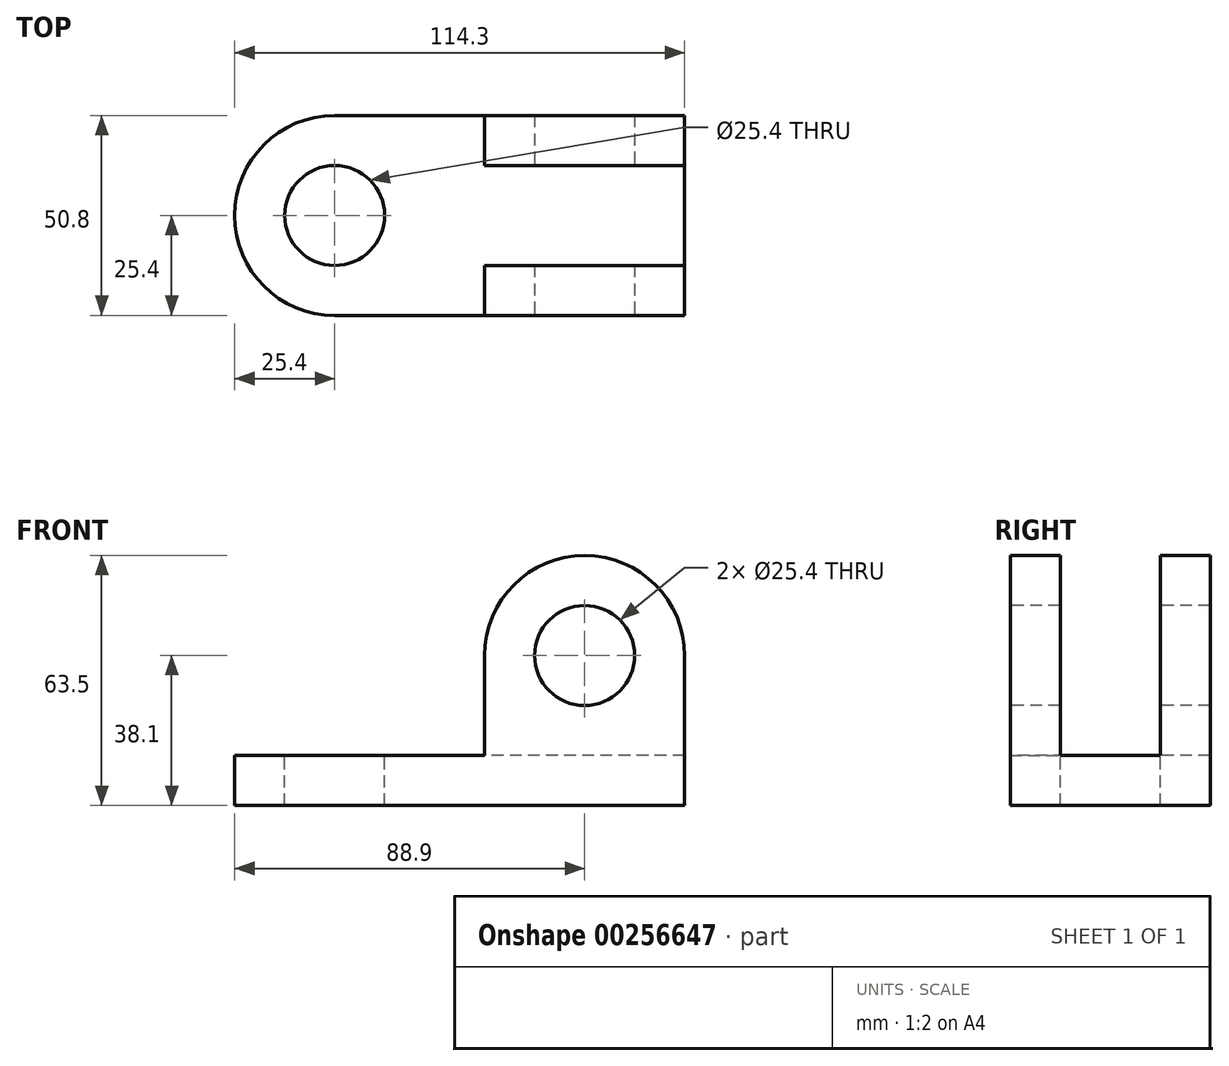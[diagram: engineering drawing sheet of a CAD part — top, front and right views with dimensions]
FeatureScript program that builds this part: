
annotation { "Feature Type Name" : "Feature", "Feature Type Description" : "" }
export const myFeature = defineFeature(function(context is Context, id is Id, definition is map)
    precondition{}
    {
        {
            var Q0;
            Q0=qCreatedBy(makeId("Top.planeOp"),FACE);
            var sketch = newSketch(context, id + "F0", { "sketchPlane" : qUnion([Q0])});
            skLineSegment(sketch, "E0.bottom", {"start": v(25.4, 0) * mm, "end": v(114.3, 0) * mm});
            skLineSegment(sketch, "E0.top", {"start": v(25.4, 50.8) * mm, "end": v(114.3, 50.8) * mm});
            skLineSegment(sketch, "E0.left", {"start": v(0, 25.4) * mm, "end": v(0, 25.4) * mm});
            skLineSegment(sketch, "E0.right", {"start": v(114.3, 0) * mm, "end": v(114.3, 50.8) * mm});
            skPoint(sketch, "E1.visualSharp", {"position": v(0, 50.8) * mm});
            skArc(sketch, "E1.filletArc", {"start": v(25.4, 50.8) * mm, "mid": v(7.44, 43.36) * mm, "end": v(0, 25.4) * mm});
            skPoint(sketch, "E2.visualSharp", {"position": v(0, 0) * mm});
            skArc(sketch, "E2.filletArc", {"start": v(0, 25.4) * mm, "mid": v(7.44, 7.44) * mm, "end": v(25.4, 0) * mm});
            skSolve(sketch);
        }
        {
            var Q0;
            Q0=makeQuery(id+"F0.imprint","IMPRINT",FACE,{"disambiguationData":[TD([[makeQuery(id+"F0.imprint","IMPRINT",EDGE,{"derivedFrom":sQuery(id+"F0.wireOp",EDGE,"E0.bottom")}),1.0]])]});
            extrude(context, id + "F1", {"entities" : qUnion([Q0]), "depth" : 12.7 * mm});
        }
        {
            var Q0;
            Q0=makeQuery(id+"F1.opExtrude","CAP_FACE",FACE,{"disambiguationData":[OSD([sQuery(id+"F0.wireOp",EDGE,"E0.bottom"),sQuery(id+"F0.wireOp",EDGE,"E0.top"),sQuery(id+"F0.wireOp",EDGE,"E0.left"),sQuery(id+"F0.wireOp",EDGE,"E0.right")])],"isStart":false});
            var sketch = newSketch(context, id + "F2", { "sketchPlane" : qUnion([Q0])});
            skLineSegment(sketch, "E3", {"start": v(0, 25.4) * mm, "end": v(114.3, 25.4) * mm, "construction": true});
            skLineSegment(sketch, "E4.bottom", {"start": v(114.3, 0) * mm, "end": v(63.5, 0) * mm});
            skLineSegment(sketch, "E4.top", {"start": v(114.3, 12.7) * mm, "end": v(63.5, 12.7) * mm});
            skLineSegment(sketch, "E4.left", {"start": v(114.3, 0) * mm, "end": v(114.3, 12.7) * mm});
            skLineSegment(sketch, "E4.right", {"start": v(63.5, 0) * mm, "end": v(63.5, 12.7) * mm});
            skLineSegment(sketch, "E5.MirrorCS", {"start": v(63.5, 50.8) * mm, "end": v(63.5, 38.1) * mm});
            skLineSegment(sketch, "E6.MirrorCS", {"start": v(114.3, 50.8) * mm, "end": v(114.3, 38.1) * mm});
            skLineSegment(sketch, "E7.MirrorCS", {"start": v(114.3, 38.1) * mm, "end": v(63.5, 38.1) * mm});
            skLineSegment(sketch, "E8.MirrorCS", {"start": v(114.3, 50.8) * mm, "end": v(63.5, 50.8) * mm});
            skPoint(sketch, "E9", {"position": v(25.4, 25.4) * mm});
            skSolve(sketch);
        }
        {
            var Q0;
            Q0=makeQuery(id+"F2.imprint","IMPRINT",FACE,{"disambiguationData":[TD([[makeQuery(id+"F2.imprint","IMPRINT",EDGE,{"derivedFrom":sQuery(id+"F2.wireOp",EDGE,"E4.bottom")}),1.0]])]});
            var Q1;
            Q1=makeQuery(id+"F2.imprint","IMPRINT",FACE,{"disambiguationData":[TD([[makeQuery(id+"F2.imprint","IMPRINT",EDGE,{"derivedFrom":sQuery(id+"F2.wireOp",EDGE,"E5.MirrorCS")}),1.0]])]});
            extrude(context, id + "F3", {"entities" : qUnion([Q0, Q1]), "operationType" : NewBodyOperationType.ADD, "depth" : 50.8 * mm});
        }
        {
            var Q0;
            Q0=sQuery(id+"F2.wireOp",VERTEX,"E9");
            var Q1;
            Q1=makeQuery(id+"F1.opExtrude","SWEPT_BODY",BODY,{"disambiguationData":[OSD([sQuery(id+"F0.wireOp",EDGE,"E0.bottom"),sQuery(id+"F0.wireOp",EDGE,"E0.top"),sQuery(id+"F0.wireOp",EDGE,"E0.right"),sQuery(id+"F0.wireOp",EDGE,"E1.filletArc"),sQuery(id+"F0.wireOp",EDGE,"E2.filletArc")])]});
            hole(context, id + "F4", {"style" : HoleStyle.SIMPLE, "endStyle" : HoleEndStyle.THROUGH, "holeDiameter" : 25.4 * mm, "tappedDepth" : 12.7 * mm, "tapClearance" : 3, "locations" : qUnion([Q0]), "scope" : qUnion([Q1])});
        }
        {
            var Q0;
            Q0=makeQuery(id+"F3.opExtrude","CAP_EDGE",EDGE,{"disambiguationData":[OSD([sQuery(id+"F2.wireOp",EDGE,"E4.right")])],"isStart":false});
            fillet(context, id + "F5", {"entities" : qUnion([Q0]), "radius" : 25.4 * mm, "tangentPropagation" : true, "allowEdgeOverflow" : false});
        }
        {
            var Q0;
            Q0=makeQuery(id+"F3.opExtrude","CAP_EDGE",EDGE,{"disambiguationData":[OSD([sQuery(id+"F2.wireOp",EDGE,"E4.left")])],"isStart":false});
            fillet(context, id + "F6", {"entities" : qUnion([Q0]), "radius" : 25.4 * mm, "tangentPropagation" : true, "allowEdgeOverflow" : false});
        }
        {
            var Q0;
            Q0=makeQuery(id+"F3.opExtrude","CAP_EDGE",EDGE,{"disambiguationData":[OSD([sQuery(id+"F2.wireOp",EDGE,"E5.MirrorCS")])],"isStart":false});
            fillet(context, id + "F7", {"entities" : qUnion([Q0]), "radius" : 25.4 * mm, "tangentPropagation" : true, "allowEdgeOverflow" : false});
        }
        {
            var Q0;
            Q0=makeQuery(id+"F3.opExtrude","CAP_EDGE",EDGE,{"disambiguationData":[OSD([sQuery(id+"F2.wireOp",EDGE,"E6.MirrorCS")])],"isStart":false});
            fillet(context, id + "F8", {"entities" : qUnion([Q0]), "radius" : 25.4 * mm, "tangentPropagation" : true, "allowEdgeOverflow" : false});
        }
        {
            var Q0;
            Q0=makeQuery(id+"F3.boolean.opBoolean","MERGE",FACE,{"derivedFrom":[makeQuery(id+"F1.opExtrude","SWEPT_FACE",FACE,{"disambiguationData":[OSD([sQuery(id+"F0.wireOp",EDGE,"E0.bottom")])]}),makeQuery(id+"F3.opExtrude","SWEPT_FACE",FACE,{"disambiguationData":[OSD([sQuery(id+"F2.wireOp",EDGE,"E4.bottom")])]})]});
            var sketch = newSketch(context, id + "F9", { "sketchPlane" : qUnion([Q0])});
            skPoint(sketch, "E10", {"position": v(88.9, 38.1) * mm});
            skSolve(sketch);
        }
        {
            var Q0;
            Q0=sQuery(id+"F9.wireOp",VERTEX,"E10");
            var Q1;
            Q1=makeQuery(id+"F1.opExtrude","SWEPT_BODY",BODY,{"disambiguationData":[OSD([sQuery(id+"F0.wireOp",EDGE,"E0.bottom"),sQuery(id+"F0.wireOp",EDGE,"E0.top"),sQuery(id+"F0.wireOp",EDGE,"E0.right"),sQuery(id+"F0.wireOp",EDGE,"E1.filletArc"),sQuery(id+"F0.wireOp",EDGE,"E2.filletArc")])]});
            hole(context, id + "F10", {"style" : HoleStyle.SIMPLE, "endStyle" : HoleEndStyle.THROUGH, "holeDiameter" : 25.4 * mm, "tappedDepth" : 12.7 * mm, "tapClearance" : 3, "locations" : qUnion([Q0]), "scope" : qUnion([Q1])});
        }
    });
